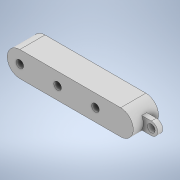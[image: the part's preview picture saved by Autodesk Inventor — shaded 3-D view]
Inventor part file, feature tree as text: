
AUTODESK INVENTOR PART (.ipt)
format: ipt  version: 2022 (Build 260153000, 153)  size: 131,584 bytes
history: native  units: mm
features: extrude x2, sketch x2, plane x1, projected_geometry x1
ambient origin geometry x8: Origin, YZ Plane, XZ Plane, XY Plane, X Axis, Y Axis, Z Axis, Center Point
bodies: Solid1 (feature_tree)
feature tree (6):
  extrude  "Extrusion1"  Depth=20.0mm
  plane  "Work Plane1"
  extrude  "Extrusion2"  Depth=20.0mm
  sketch  "Sketch1"  dims[d0=20.0mm d3=6.0mm]
  sketch  "Sketch2"  dims[d5=6.0mm d6=20.0mm d7=0.0mm d8=10.0mm d9=6.0mm d10=4.0mm d11=0.0mm d16=30.0mm d17=30.0mm d18=80.0mm]
  projected_geometry  "Projected Loop1"
